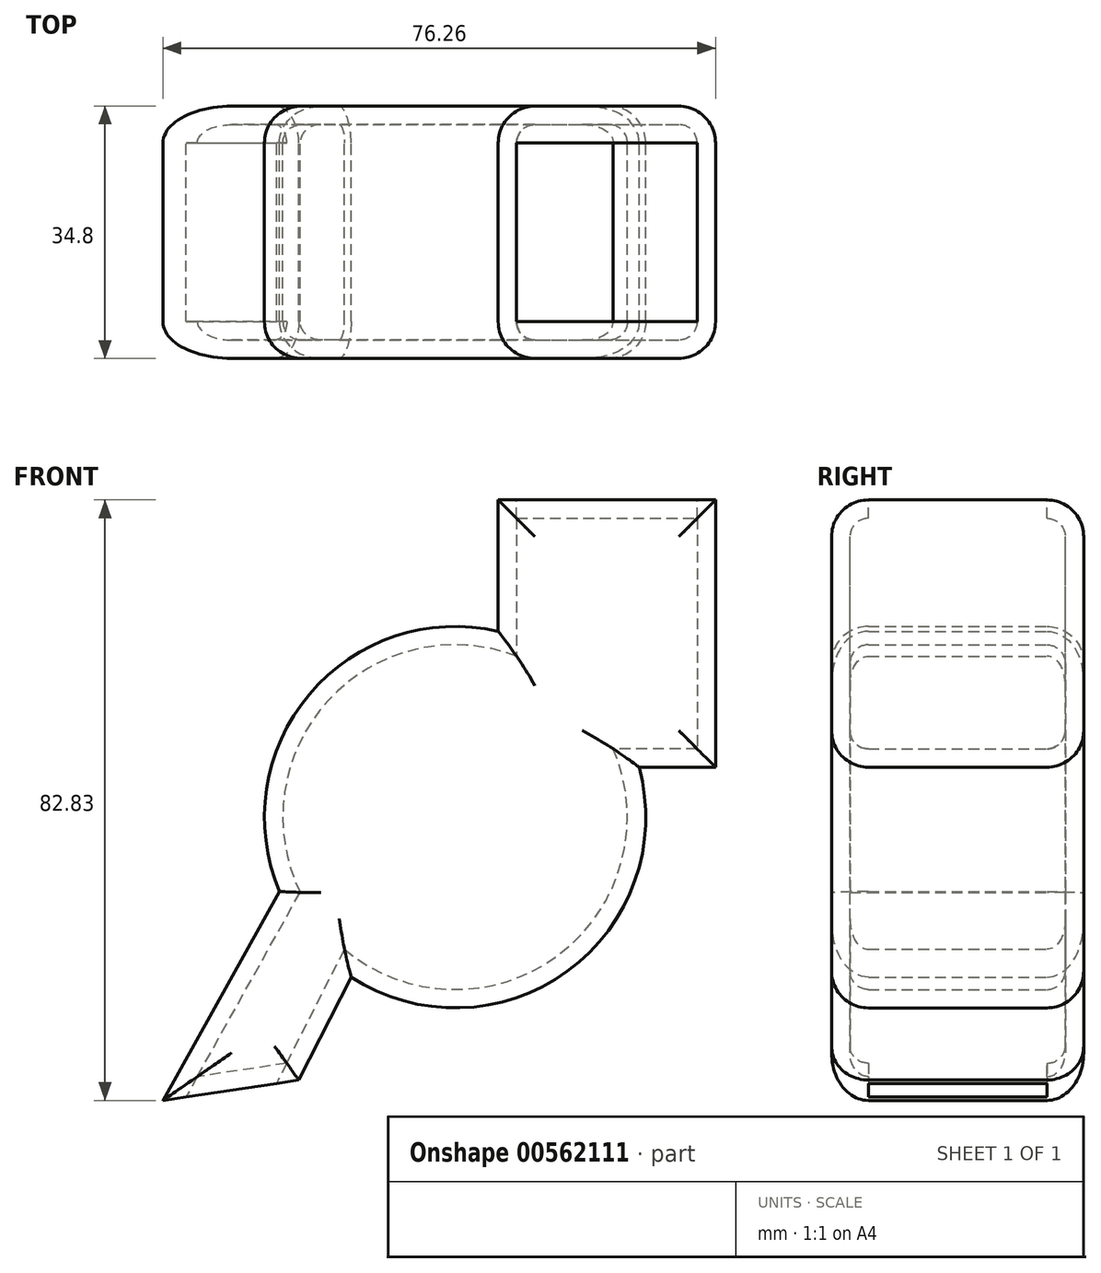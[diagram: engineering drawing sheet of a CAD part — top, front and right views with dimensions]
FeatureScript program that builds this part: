
annotation { "Feature Type Name" : "Feature", "Feature Type Description" : "" }
export const myFeature = defineFeature(function(context is Context, id is Id, definition is map)
    precondition{}
    {
        {
            var Q0;
            Q0=qCreatedBy(makeId("Front.planeOp"),FACE);
            var sketch = newSketch(context, id + "F0", { "sketchPlane" : qUnion([Q0])});
            skArc(sketch, "E0", {"start": v(5.94, 25.63) * mm, "mid": v(-20.14, 16.93) * mm, "end": v(-24.23, -10.26) * mm});
            skLineSegment(sketch, "E1.bottom", {"start": v(35.94, 43.76) * mm, "end": v(5.94, 43.76) * mm});
            skLineSegment(sketch, "E1.top", {"start": v(35.94, 6.88) * mm, "end": v(25.4, 6.88) * mm});
            skLineSegment(sketch, "E1.left", {"start": v(35.94, 43.76) * mm, "end": v(35.94, 6.88) * mm});
            skLineSegment(sketch, "E1.right", {"start": v(5.94, 43.76) * mm, "end": v(5.94, 25.63) * mm});
            skPoint(sketch, "E1.middle", {"position": v(20.94, 25.32) * mm});
            skLineSegment(sketch, "E2", {"start": v(-40.32, -39.07) * mm, "end": v(-21.57, -36.25) * mm});
            skLineSegment(sketch, "E3", {"start": v(-21.57, -36.25) * mm, "end": v(-14.35, -22.05) * mm});
            skLineSegment(sketch, "E4", {"start": v(-40.32, -39.07) * mm, "end": v(-24.23, -10.26) * mm});
            skPoint(sketch, "E5.orphan", {"position": v(5.94, 6.88) * mm});
            skArc(sketch, "E6.trimOffspring", {"start": v(-14.35, -22.05) * mm, "mid": v(15.48, -21.27) * mm, "end": v(25.4, 6.88) * mm});
            skSolve(sketch);
        }
        {
            var Q0;
            Q0 = qSketchRegion(id + "F0", true);
            extrude(context, id + "F1", {"entities" : qUnion([Q0]), "depth" : 34.8 * mm, "offsetDistance" : 25.4 * mm});
        }
        {
            var Q0;
            Q0=makeQuery(id+"F1.opExtrude","CAP_FACE",FACE,{"disambiguationData":[OSD([sQuery(id+"F0.wireOp",EDGE,"E0"),sQuery(id+"F0.wireOp",EDGE,"E1.bottom"),sQuery(id+"F0.wireOp",EDGE,"E1.top"),sQuery(id+"F0.wireOp",EDGE,"E1.left"),sQuery(id+"F0.wireOp",EDGE,"E1.right"),sQuery(id+"F0.wireOp",EDGE,"E2"),sQuery(id+"F0.wireOp",EDGE,"E3"),sQuery(id+"F0.wireOp",EDGE,"E4"),sQuery(id+"F0.wireOp",EDGE,"E6.trimOffspring")])],"isStart":false});
            var Q1;
            Q1=makeQuery(id+"F1.opExtrude","CAP_FACE",FACE,{"disambiguationData":[OSD([sQuery(id+"F0.wireOp",EDGE,"E0"),sQuery(id+"F0.wireOp",EDGE,"E1.bottom"),sQuery(id+"F0.wireOp",EDGE,"E1.top"),sQuery(id+"F0.wireOp",EDGE,"E1.left"),sQuery(id+"F0.wireOp",EDGE,"E1.right"),sQuery(id+"F0.wireOp",EDGE,"E2"),sQuery(id+"F0.wireOp",EDGE,"E3"),sQuery(id+"F0.wireOp",EDGE,"E4"),sQuery(id+"F0.wireOp",EDGE,"E6.trimOffspring")])],"isStart":true});
            fillet(context, id + "F2", {"entities" : qUnion([Q0, Q1]), "radius" : 5.08 * mm, "tangentPropagation" : true, "allowEdgeOverflow" : false});
        }
        {
            var Q0;
            Q0=makeQuery(id+"F1.opExtrude","SWEPT_FACE",FACE,{"disambiguationData":[OSD([sQuery(id+"F0.wireOp",EDGE,"E1.bottom")])]});
            var Q1;
            Q1=makeQuery(id+"F1.opExtrude","SWEPT_FACE",FACE,{"disambiguationData":[OSD([sQuery(id+"F0.wireOp",EDGE,"E2")])]});
            shell(context, id + "F3", {"entities" : qUnion([Q0, Q1]), "thickness" : 2.54 * mm});
        }
    });
